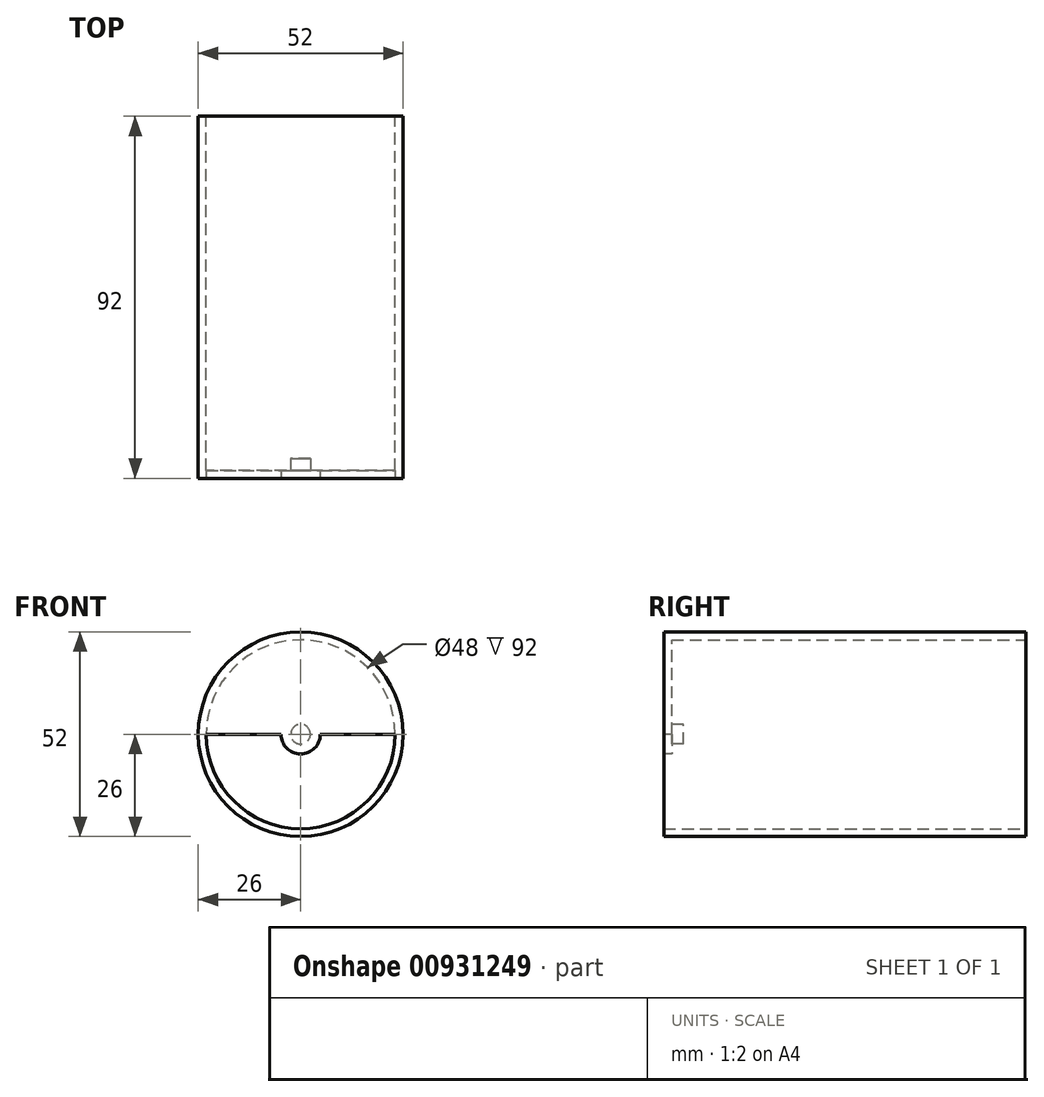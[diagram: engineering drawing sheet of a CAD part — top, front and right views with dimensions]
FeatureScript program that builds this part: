
annotation { "Feature Type Name" : "Feature", "Feature Type Description" : "" }
export const myFeature = defineFeature(function(context is Context, id is Id, definition is map)
    precondition{}
    {
        {
            var Q0;
            Q0=qCreatedBy(makeId("Front.planeOp"),FACE);
            var sketch = newSketch(context, id + "F0", { "sketchPlane" : qUnion([Q0])});
            skCircle(sketch, "E0", {"center": v(0, 0) * mm, "radius": 26 * mm});
            skCircle(sketch, "E1", {"center": v(0, 0) * mm, "radius": 24 * mm});
            skSolve(sketch);
        }
        {
            var Q0;
            Q0=makeQuery(id+"F0.imprint","IMPRINT",FACE,{"disambiguationData":[TD([[makeQuery(id+"F0.imprint","IMPRINT",EDGE,{"derivedFrom":sQuery(id+"F0.wireOp",EDGE,"E1")}),1.0]])]});
            var Q1;
            Q1=makeQuery(id+"F0.imprint","IMPRINT",FACE,{"disambiguationData":[TD([[makeQuery(id+"F0.imprint","IMPRINT",EDGE,{"derivedFrom":sQuery(id+"F0.wireOp",EDGE,"E0")}),1.0]])]});
            extrude(context, id + "F1", {"entities" : qUnion([Q0, Q1]), "depth" : 42 * mm, "offsetDistance" : 25 * mm});
        }
        {
            var Q0;
            Q0=makeQuery(id+"F0.imprint","IMPRINT",FACE,{"disambiguationData":[TD([[makeQuery(id+"F0.imprint","IMPRINT",EDGE,{"derivedFrom":sQuery(id+"F0.wireOp",EDGE,"E1")}),1.0]])]});
            extrude(context, id + "F2", {"entities" : qUnion([Q0]), "operationType" : NewBodyOperationType.REMOVE, "depth" : 40 * mm, "offsetDistance" : 25 * mm});
        }
        {
            var Q0;
            Q0=makeQuery(id+"F1.opExtrude","CAP_FACE",FACE,{"disambiguationData":[OSD([sQuery(id+"F0.wireOp",EDGE,"E0")])],"isStart":true});
            extrude(context, id + "F3", {"entities" : qUnion([Q0]), "operationType" : NewBodyOperationType.ADD, "depth" : 50 * mm, "offsetDistance" : 25 * mm});
        }
        {
            var Q0;
            Q0=makeQuery(id+"F1.opExtrude","CAP_FACE",FACE,{"disambiguationData":[OSD([sQuery(id+"F0.wireOp",EDGE,"E0")])],"isStart":false});
            var sketch = newSketch(context, id + "F4", { "sketchPlane" : qUnion([Q0])});
            skCircle(sketch, "E2", {"center": v(0, 0) * mm, "radius": 2.5 * mm});
            skArc(sketch, "E3.0", {"start": v(-24, 0) * mm, "mid": v(0, -24) * mm, "end": v(24, 0) * mm});
            skArc(sketch, "E4", {"start": v(-5, 0) * mm, "mid": v(0, -5) * mm, "end": v(5, 0) * mm});
            skLineSegment(sketch, "E5", {"start": v(5, 0) * mm, "end": v(24, 0) * mm});
            skLineSegment(sketch, "E6", {"start": v(-24, 0) * mm, "end": v(-5, 0) * mm});
            skSolve(sketch);
        }
        {
            var Q0;
            Q0=makeQuery(id+"F4.imprint","IMPRINT",FACE,{"disambiguationData":[TD([[makeQuery(id+"F4.imprint","IMPRINT",EDGE,{"derivedFrom":sQuery(id+"F4.wireOp",EDGE,"E3.0")}),1.0]])]});
            extrude(context, id + "F5", {"entities" : qUnion([Q0]), "operationType" : NewBodyOperationType.REMOVE, "endBound" : BoundingType.THROUGH_ALL, "oppositeDirection" : true, "depth" : 25 * mm, "offsetDistance" : 25 * mm});
        }
        {
            var Q0;
            Q0=makeQuery(id+"F4.imprint","IMPRINT",FACE,{"disambiguationData":[TD([[makeQuery(id+"F4.imprint","IMPRINT",EDGE,{"derivedFrom":sQuery(id+"F4.wireOp",EDGE,"E2")}),1.0]])]});
            extrude(context, id + "F6", {"entities" : qUnion([Q0]), "operationType" : NewBodyOperationType.ADD, "oppositeDirection" : true, "depth" : 5 * mm, "offsetDistance" : 25 * mm});
        }
    });
